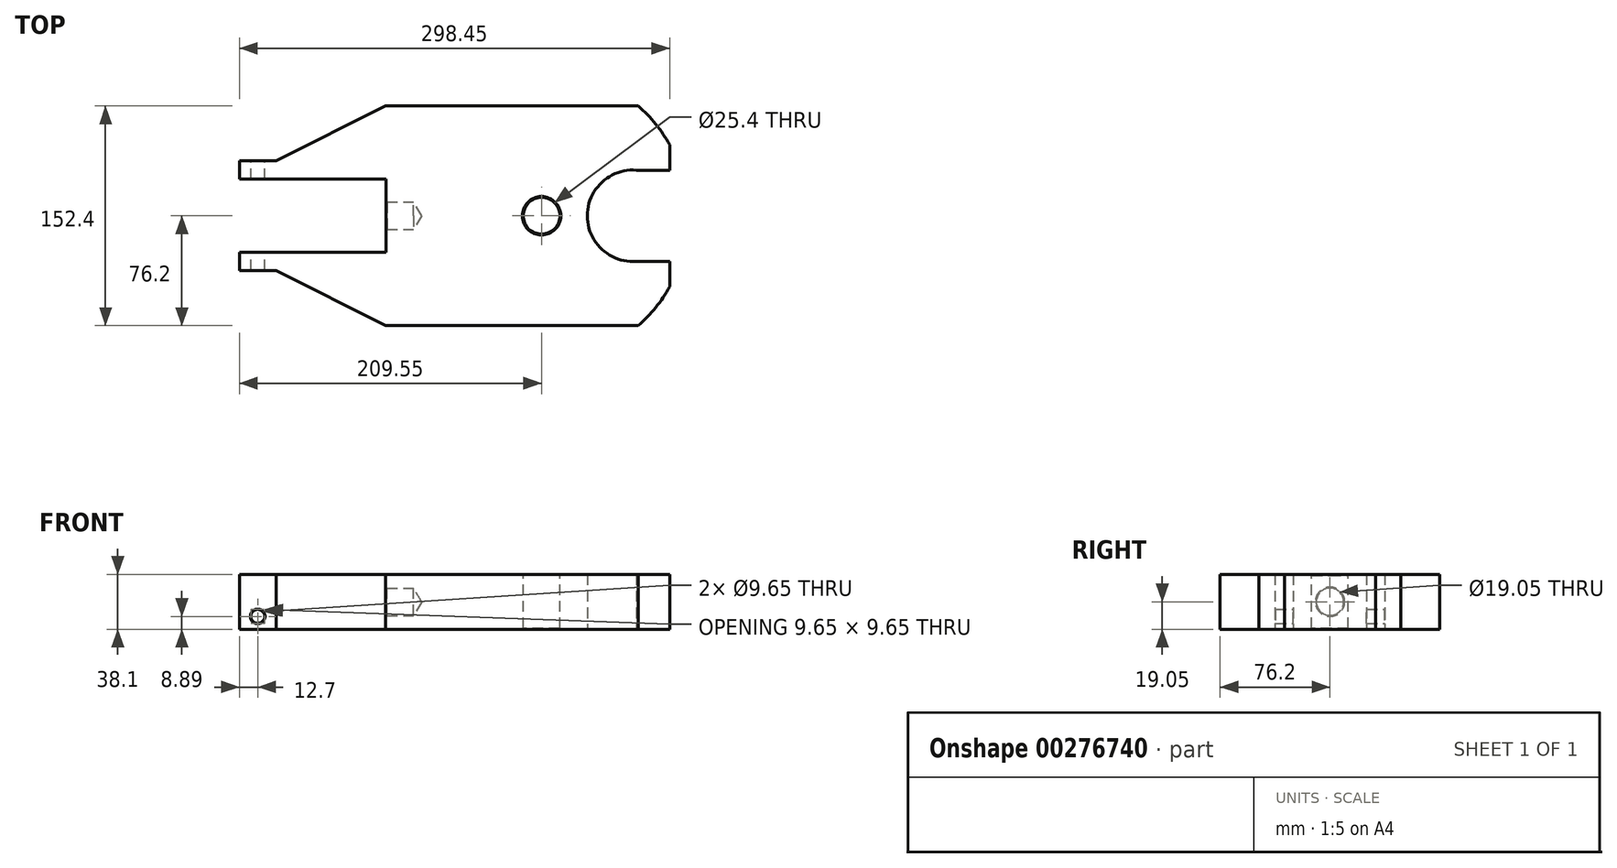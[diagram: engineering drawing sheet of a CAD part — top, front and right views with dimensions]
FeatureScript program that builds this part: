
annotation { "Feature Type Name" : "Feature", "Feature Type Description" : "" }
export const myFeature = defineFeature(function(context is Context, id is Id, definition is map)
    precondition{}
    {
        {
            var Q0;
            Q0=qCreatedBy(makeId("Top.planeOp"),FACE);
            var sketch = newSketch(context, id + "F0", { "sketchPlane" : qUnion([Q0])});
            skLineSegment(sketch, "E0", {"start": v(0, 0) * mm, "end": v(0, 25.4) * mm});
            skLineSegment(sketch, "E1", {"start": v(0, 25.4) * mm, "end": v(-101.6, 25.4) * mm});
            skLineSegment(sketch, "E2", {"start": v(-101.6, 25.4) * mm, "end": v(-101.6, 38.1) * mm});
            skLineSegment(sketch, "E3", {"start": v(-101.6, 38.1) * mm, "end": v(-76.2, 38.1) * mm});
            skLineSegment(sketch, "E4", {"start": v(-76.2, 38.1) * mm, "end": v(-0.12, 76.2) * mm});
            skLineSegment(sketch, "E5", {"start": v(-0.12, 76.2) * mm, "end": v(175.15, 76.2) * mm});
            skArc(sketch, "E6", {"start": v(196.85, 49.19) * mm, "mid": v(187.16, 63.63) * mm, "end": v(175.15, 76.2) * mm});
            skLineSegment(sketch, "E7", {"start": v(196.85, 49.19) * mm, "end": v(196.85, 31.66) * mm});
            skLineSegment(sketch, "E8", {"start": v(196.85, 31.66) * mm, "end": v(171.45, 31.66) * mm});
            skLineSegment(sketch, "E9", {"start": v(0, 0) * mm, "end": v(279.8, 0) * mm, "construction": true});
            skLineSegment(sketch, "E10.MirrorCS", {"start": v(0, 0) * mm, "end": v(0, -25.4) * mm});
            skLineSegment(sketch, "E11.MirrorCS", {"start": v(0, -25.4) * mm, "end": v(-101.6, -25.4) * mm});
            skLineSegment(sketch, "E12.MirrorCS", {"start": v(-101.6, -25.4) * mm, "end": v(-101.6, -38.1) * mm});
            skLineSegment(sketch, "E13.MirrorCS", {"start": v(-101.6, -38.1) * mm, "end": v(-76.2, -38.1) * mm});
            skLineSegment(sketch, "E14.MirrorCS", {"start": v(-76.2, -38.1) * mm, "end": v(-0.12, -76.2) * mm});
            skLineSegment(sketch, "E15.MirrorCS", {"start": v(-0.12, -76.2) * mm, "end": v(175.15, -76.2) * mm});
            skArc(sketch, "E16.MirrorCS", {"start": v(196.85, -49.19) * mm, "mid": v(187.16, -63.63) * mm, "end": v(175.15, -76.2) * mm});
            skLineSegment(sketch, "E17.MirrorCS", {"start": v(196.85, -49.19) * mm, "end": v(196.85, -31.66) * mm});
            skLineSegment(sketch, "E18.MirrorCS", {"start": v(196.85, -31.66) * mm, "end": v(171.45, -31.66) * mm});
            skArc(sketch, "E19", {"start": v(173.83, 31.66) * mm, "mid": v(139.7, 0) * mm, "end": v(173.83, -31.66) * mm});
            skSolve(sketch);
        }
        {
            var Q0;
            Q0 = qSketchRegion(id + "F0", true);
            extrude(context, id + "F1", {"entities" : qUnion([Q0]), "depth" : 38.1 * mm});
        }
        {
            var Q0;
            Q0=makeQuery(id+"F1.opExtrude","SWEPT_FACE",FACE,{"disambiguationData":[OSD([sQuery(id+"F0.wireOp",EDGE,"E0"),sQuery(id+"F0.wireOp",EDGE,"E10.MirrorCS")])]});
            cPlane(context, id + "F2", {"entities" : qUnion([Q0]), "cplaneType" : CPlaneType.OFFSET, "offset" : 107.95 * mm, "oppositeDirection" : true, "width" : 152.4 * mm, "height" : 152.4 * mm});
        }
        {
            var Q0;
            Q0=qCreatedBy(id+"F2.planeOp",FACE);
            var sketch = newSketch(context, id + "F3", { "sketchPlane" : qUnion([Q0])});
            skLineSegment(sketch, "E20", {"start": v(76.2, 38.1) * mm, "end": v(-76.2, 38.1) * mm, "construction": true});
            skLineSegment(sketch, "E21", {"start": v(76.2, 38.1) * mm, "end": v(76.2, 0) * mm, "construction": true});
            skLineSegment(sketch, "E22", {"start": v(-76.2, 38.1) * mm, "end": v(-76.2, 0) * mm, "construction": true});
            skLineSegment(sketch, "E23", {"start": v(76.2, 0) * mm, "end": v(-76.2, 0) * mm, "construction": true});
            skLineSegment(sketch, "E24", {"start": v(0, 0) * mm, "end": v(0, 38.1) * mm, "construction": true});
            skLineSegment(sketch, "E25", {"start": v(76.2, 19.05) * mm, "end": v(-76.2, 19.05) * mm, "construction": true});
            skLineSegment(sketch, "E26", {"start": v(0, 0) * mm, "end": v(0, 38.1) * mm});
            skLineSegment(sketch, "E27", {"start": v(0, 38.1) * mm, "end": v(-13.34, 38.1) * mm});
            skLineSegment(sketch, "E28", {"start": v(-13.34, 38.1) * mm, "end": v(-12.7, 37.47) * mm});
            skLineSegment(sketch, "E29", {"start": v(0, 0) * mm, "end": v(-13.34, 0) * mm});
            skLineSegment(sketch, "E30", {"start": v(-12.7, 0.64) * mm, "end": v(-13.34, 0) * mm});
            skLineSegment(sketch, "E31", {"start": v(-12.7, 0.64) * mm, "end": v(-12.7, 37.47) * mm});
            skLineSegment(sketch, "E32.MirrorCS", {"start": v(13.33, 38.1) * mm, "end": v(12.7, 37.47) * mm});
            skLineSegment(sketch, "E33.MirrorCS", {"start": v(12.7, 0.64) * mm, "end": v(13.33, 0) * mm});
            skSolve(sketch);
        }
        {
            var Q0;
            Q0 = qSketchRegion(id + "F3", true);
            var Q1;
            Q1=sQuery(id+"F3.wireOp",EDGE,"E26");
            revolve(context, id + "F4", {"operationType" : NewBodyOperationType.REMOVE, "entities" : qUnion([Q0]), "axis" : qUnion([Q1]), "revolveType" : RevolveType.FULL, "oppositeDirection" : true});
        }
        {
            var Q0;
            Q0=makeQuery(id+"F1.opExtrude","CAP_FACE",FACE,{"disambiguationData":[OSD([sQuery(id+"F0.wireOp",EDGE,"E0"),sQuery(id+"F0.wireOp",EDGE,"E1"),sQuery(id+"F0.wireOp",EDGE,"E2"),sQuery(id+"F0.wireOp",EDGE,"E3"),sQuery(id+"F0.wireOp",EDGE,"E4"),sQuery(id+"F0.wireOp",EDGE,"E5"),sQuery(id+"F0.wireOp",EDGE,"E6"),sQuery(id+"F0.wireOp",EDGE,"E7"),sQuery(id+"F0.wireOp",EDGE,"E8"),sQuery(id+"F0.wireOp",EDGE,"E10.MirrorCS"),sQuery(id+"F0.wireOp",EDGE,"E11.MirrorCS"),sQuery(id+"F0.wireOp",EDGE,"E12.MirrorCS"),sQuery(id+"F0.wireOp",EDGE,"E13.MirrorCS"),sQuery(id+"F0.wireOp",EDGE,"E14.MirrorCS"),sQuery(id+"F0.wireOp",EDGE,"E15.MirrorCS"),sQuery(id+"F0.wireOp",EDGE,"E16.MirrorCS"),sQuery(id+"F0.wireOp",EDGE,"E17.MirrorCS"),sQuery(id+"F0.wireOp",EDGE,"E18.MirrorCS"),sQuery(id+"F0.wireOp",EDGE,"E19")])],"isStart":false});
            var Q1;
            Q1=makeQuery(id+"F1.opExtrude","CAP_FACE",FACE,{"disambiguationData":[OSD([sQuery(id+"F0.wireOp",EDGE,"E0"),sQuery(id+"F0.wireOp",EDGE,"E1"),sQuery(id+"F0.wireOp",EDGE,"E2"),sQuery(id+"F0.wireOp",EDGE,"E3"),sQuery(id+"F0.wireOp",EDGE,"E4"),sQuery(id+"F0.wireOp",EDGE,"E5"),sQuery(id+"F0.wireOp",EDGE,"E6"),sQuery(id+"F0.wireOp",EDGE,"E7"),sQuery(id+"F0.wireOp",EDGE,"E8"),sQuery(id+"F0.wireOp",EDGE,"E10.MirrorCS"),sQuery(id+"F0.wireOp",EDGE,"E11.MirrorCS"),sQuery(id+"F0.wireOp",EDGE,"E12.MirrorCS"),sQuery(id+"F0.wireOp",EDGE,"E13.MirrorCS"),sQuery(id+"F0.wireOp",EDGE,"E14.MirrorCS"),sQuery(id+"F0.wireOp",EDGE,"E15.MirrorCS"),sQuery(id+"F0.wireOp",EDGE,"E16.MirrorCS"),sQuery(id+"F0.wireOp",EDGE,"E17.MirrorCS"),sQuery(id+"F0.wireOp",EDGE,"E18.MirrorCS"),sQuery(id+"F0.wireOp",EDGE,"E19")])],"isStart":true});
            cPlane(context, id + "F5", {"entities" : qUnion([Q0, Q1]), "cplaneType" : CPlaneType.MID_PLANE, "offset" : 25.4 * mm, "width" : 152.4 * mm, "height" : 152.4 * mm});
        }
        {
            var Q0;
            Q0=qCreatedBy(id+"F5.planeOp",FACE);
            var sketch = newSketch(context, id + "F6", { "sketchPlane" : qUnion([Q0])});
            skLineSegment(sketch, "E34", {"start": v(-101.6, 25.4) * mm, "end": v(0, 25.4) * mm, "construction": true});
            skLineSegment(sketch, "E35", {"start": v(0, 25.4) * mm, "end": v(0, -25.4) * mm, "construction": true});
            skLineSegment(sketch, "E36", {"start": v(-101.6, -25.4) * mm, "end": v(0, -25.4) * mm, "construction": true});
            skLineSegment(sketch, "E37", {"start": v(0, 0) * mm, "end": v(-123.9, 0) * mm, "construction": true});
            skPoint(sketch, "E37.endSnap0", {"position": v(0, 0) * mm});
            skLineSegment(sketch, "E38", {"start": v(0, 0) * mm, "end": v(0, -10.16) * mm});
            skLineSegment(sketch, "E39", {"start": v(0, -10.16) * mm, "end": v(0.63, -9.52) * mm});
            skLineSegment(sketch, "E40", {"start": v(0, 0) * mm, "end": v(24.77, 0) * mm});
            skLineSegment(sketch, "E41", {"start": v(24.77, 0) * mm, "end": v(19.05, -9.53) * mm});
            skLineSegment(sketch, "E42", {"start": v(19.05, -9.53) * mm, "end": v(0.63, -9.53) * mm});
            skLineSegment(sketch, "E43.MirrorCS", {"start": v(0, 10.16) * mm, "end": v(0.63, 9.53) * mm});
            skLineSegment(sketch, "E44.MirrorCS", {"start": v(24.77, 0) * mm, "end": v(19.05, 9.53) * mm, "construction": true});
            skSolve(sketch);
        }
        {
            var Q0;
            Q0 = qSketchRegion(id + "F6", true);
            var Q1;
            Q1=sQuery(id+"F6.wireOp",EDGE,"E40");
            revolve(context, id + "F7", {"operationType" : NewBodyOperationType.REMOVE, "entities" : qUnion([Q0]), "axis" : qUnion([Q1]), "revolveType" : RevolveType.FULL, "oppositeDirection" : true});
        }
        {
            var Q0;
            Q0=makeQuery(id+"F1.opExtrude","SWEPT_FACE",FACE,{"disambiguationData":[OSD([sQuery(id+"F0.wireOp",EDGE,"E12.MirrorCS")])]});
            cPlane(context, id + "F8", {"entities" : qUnion([Q0]), "cplaneType" : CPlaneType.OFFSET, "offset" : 12.7 * mm, "oppositeDirection" : true, "width" : 152.4 * mm, "height" : 152.4 * mm});
        }
        {
            var Q0;
            Q0=qCreatedBy(id+"F8.planeOp",FACE);
            var sketch = newSketch(context, id + "F9", { "sketchPlane" : qUnion([Q0])});
            skLineSegment(sketch, "E45", {"start": v(-25.4, 0) * mm, "end": v(-25.4, 38.1) * mm, "construction": true});
            skLineSegment(sketch, "E46", {"start": v(38.1, 38.1) * mm, "end": v(38.1, 0) * mm, "construction": true});
            skLineSegment(sketch, "E47", {"start": v(-25.4, 38.1) * mm, "end": v(-38.1, 38.1) * mm, "construction": true});
            skLineSegment(sketch, "E48", {"start": v(38.1, 38.1) * mm, "end": v(25.4, 38.1) * mm, "construction": true});
            skLineSegment(sketch, "E49", {"start": v(25.4, 0) * mm, "end": v(25.4, 38.1) * mm, "construction": true});
            skLineSegment(sketch, "E50", {"start": v(-38.1, 38.1) * mm, "end": v(-38.1, 0) * mm, "construction": true});
            skLineSegment(sketch, "E51", {"start": v(-25.4, 0) * mm, "end": v(-38.1, 0) * mm, "construction": true});
            skLineSegment(sketch, "E52", {"start": v(38.1, 0) * mm, "end": v(25.4, 0) * mm, "construction": true});
            skLineSegment(sketch, "E53", {"start": v(-38.1, 8.89) * mm, "end": v(38.1, 8.9) * mm, "construction": true});
            skLineSegment(sketch, "E54", {"start": v(-38.1, 8.89) * mm, "end": v(-38.1, 3.8) * mm});
            skLineSegment(sketch, "E55", {"start": v(-38.1, 3.8) * mm, "end": v(-37.85, 4.06) * mm});
            skLineSegment(sketch, "E56", {"start": v(-37.85, 4.06) * mm, "end": v(37.85, 4.06) * mm});
            skLineSegment(sketch, "E57", {"start": v(37.85, 4.06) * mm, "end": v(38.1, 3.8) * mm});
            skLineSegment(sketch, "E58", {"start": v(38.1, 3.81) * mm, "end": v(38.1, 8.9) * mm});
            skLineSegment(sketch, "E59", {"start": v(38.1, 8.9) * mm, "end": v(-38.1, 8.89) * mm});
            skLineSegment(sketch, "E60.0", {"start": v(25.4, 38.1) * mm, "end": v(-25.4, 38.1) * mm, "construction": true});
            skLineSegment(sketch, "E61.0", {"start": v(25.4, 0) * mm, "end": v(-25.4, 0) * mm, "construction": true});
            skLineSegment(sketch, "E62", {"start": v(0, 0) * mm, "end": v(0, 38.1) * mm, "construction": true});
            skLineSegment(sketch, "E63.MirrorCS", {"start": v(-38.1, 13.97) * mm, "end": v(-37.85, 13.72) * mm});
            skLineSegment(sketch, "E64.MirrorCS", {"start": v(37.85, 13.72) * mm, "end": v(38.1, 13.97) * mm});
            skSolve(sketch);
        }
        {
            var Q0;
            Q0=makeQuery(id+"F9.imprint","IMPRINT",FACE,{"disambiguationData":[TD([[makeQuery(id+"F9.imprint","IMPRINT",EDGE,{"derivedFrom":sQuery(id+"F9.wireOp",EDGE,"E54")}),1.0]])]});
            var Q1;
            Q1=sQuery(id+"F9.wireOp",EDGE,"E59");
            revolve(context, id + "F10", {"operationType" : NewBodyOperationType.REMOVE, "entities" : qUnion([Q0]), "axis" : qUnion([Q1]), "revolveType" : RevolveType.FULL, "oppositeDirection" : true});
        }
    });
